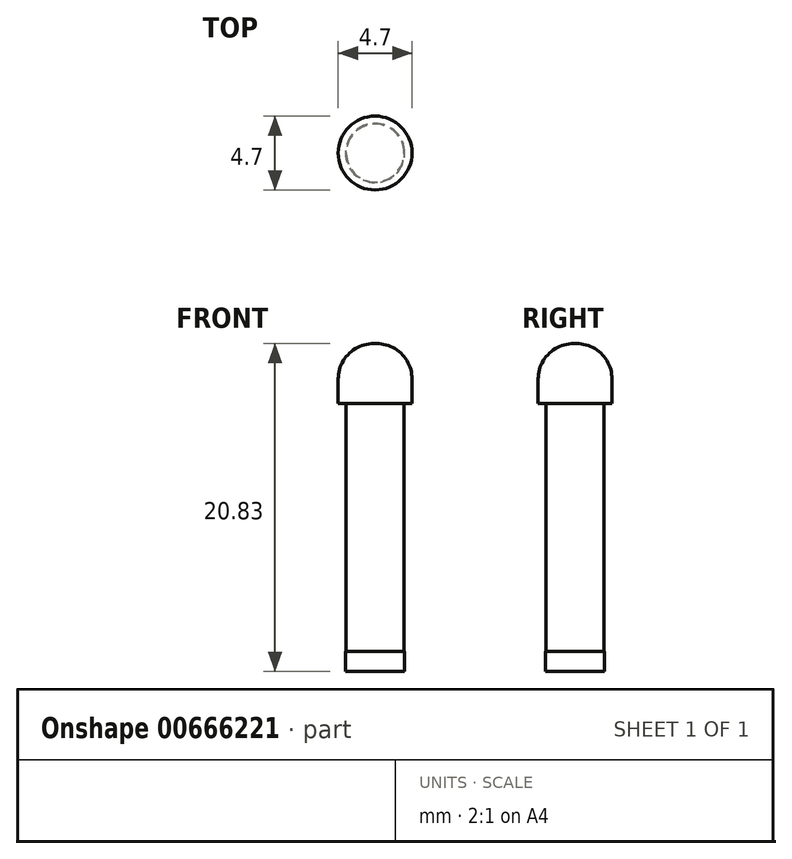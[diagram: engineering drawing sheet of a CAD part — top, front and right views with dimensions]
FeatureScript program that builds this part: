
annotation { "Feature Type Name" : "Feature", "Feature Type Description" : "" }
export const myFeature = defineFeature(function(context is Context, id is Id, definition is map)
    precondition{}
    {
        {
            var Q0;
            Q0=qCreatedBy(makeId("Top.planeOp"),FACE);
            var sketch = newSketch(context, id + "F0", { "sketchPlane" : qUnion([Q0])});
            skCircle(sketch, "E0", {"center": v(0, 0) * mm, "radius": 1.84 * mm});
            skSolve(sketch);
        }
        {
            var Q0;
            Q0=makeQuery(id+"F0.imprint","IMPRINT",FACE,{"disambiguationData":[TD([[makeQuery(id+"F0.imprint","IMPRINT",EDGE,{"derivedFrom":sQuery(id+"F0.wireOp",EDGE,"E0")}),1.0]])]});
            extrude(context, id + "F1", {"entities" : qUnion([Q0]), "depth" : 15.75 * mm, "offsetDistance" : 25.4 * mm});
        }
        {
            var Q0;
            Q0=makeQuery(id+"F1.opExtrude","CAP_FACE",FACE,{"disambiguationData":[OSD([sQuery(id+"F0.wireOp",EDGE,"E0")])],"isStart":false});
            var sketch = newSketch(context, id + "F2", { "sketchPlane" : qUnion([Q0])});
            skCircle(sketch, "E1", {"center": v(0, 0) * mm, "radius": 2.35 * mm});
            skSolve(sketch);
        }
        {
            var Q0;
            Q0 = qSketchRegion(id + "F2", true);
            extrude(context, id + "F3", {"entities" : qUnion([Q0]), "depth" : 3.8 * mm, "offsetDistance" : 25.4 * mm});
        }
        {
            var Q0;
            Q0=makeQuery(id+"F3.opExtrude","CAP_FACE",FACE,{"disambiguationData":[OSD([sQuery(id+"F2.wireOp",EDGE,"E1")])],"isStart":false});
            fillet(context, id + "F4", {"entities" : qUnion([Q0]), "radius" : 2.26 * mm, "tangentPropagation" : true, "allowEdgeOverflow" : false});
        }
        {
            var Q0;
            Q0=makeQuery(id+"F1.opExtrude","CAP_FACE",FACE,{"disambiguationData":[OSD([sQuery(id+"F0.wireOp",EDGE,"E0")])],"isStart":true});
            var sketch = newSketch(context, id + "F5", { "sketchPlane" : qUnion([Q0])});
            skCircle(sketch, "E2", {"center": v(0, 0) * mm, "radius": 1.88 * mm});
            skSolve(sketch);
        }
        {
            var Q0;
            Q0 = qSketchRegion(id + "F5", true);
            extrude(context, id + "F6", {"entities" : qUnion([Q0]), "depth" : 1.27 * mm, "offsetDistance" : 25.4 * mm});
        }
    });
